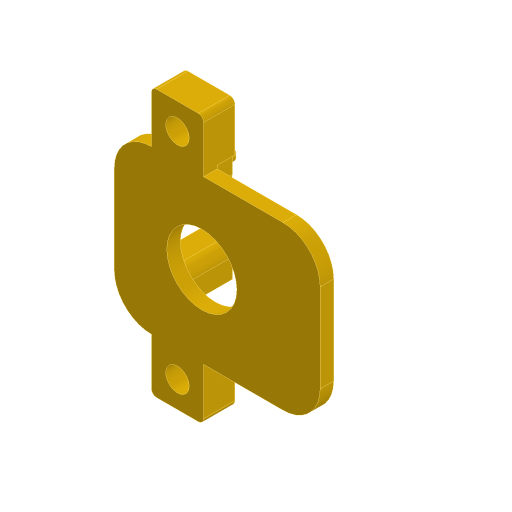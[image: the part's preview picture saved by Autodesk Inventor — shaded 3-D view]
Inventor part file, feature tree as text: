
AUTODESK INVENTOR PART (.ipt)
format: ipt  version: 2024.3 (Build 283343000, 343)  size: 441,344 bytes
history: native  units: mm
features: reference x10, sketch x6, extrude x6, other x4, plane x2, projected_geometry x2, fillet x1, chamfer x1, mirror x1
ambient origin geometry x8: Origin, YZ Plane, XZ Plane, XY Plane, X Axis, Y Axis, Z Axis, Center Point
bodies: Solid1 (feature_tree)
feature tree (33):
  plane  "Work Plane1"
  sketch  "Sketch1"  dims[d0=0.6mm d1=1.0mm d2=1.0mm]
  plane  "Work Plane2"
  extrude  "Extrusion1"  Depth=1.0mm
  fillet  "Fillet1"  Radius=1.0mm
  extrude  "Extrusion2"  Depth=2.0mm
  chamfer  "Chamfer1"  Distance=3.0mm
  extrude  "Extrusion3"  Depth=2.6mm TaperAngle=0.0deg
  extrude  "Extrusion4"  TaperAngle=0.0deg  [1 undecoded]
  extrude  "Extrusion5"  Depth=0.6mm TaperAngle=0.0deg
  extrude  "Extrusion6"  [1 undecoded]
  mirror  "Mirror1"
  reference  "Reference1"
  reference  "Reference2"
  reference  "Reference3"
  sketch  "Sketch2"  dims[d3=10.0mm d4=0.0mm d5=2.0mm d6=3.0mm d7=0.0mm]
  reference  "Reference4"
  reference  "Reference5"
  sketch  "Sketch3"  dims[d8=0.6mm d9=2.0mm d10=45.0deg d11=2.6mm d12=0.0mm]
  reference  "Reference6"
  reference  "Reference7"
  sketch  "Sketch4"  dims[d13=1.0mm d14=0.0mm d15=0.0mm]
  reference  "Reference8"
  sketch  "Sketch5"  dims[d16=6.0mm d17=0.0mm d18=0.6mm d19=0.0mm]
  projected_geometry  "Projected Loop1"
  reference  "Reference9"
  reference  "Reference10"
  sketch  "Sketch6"
  projected_geometry  "Projected Loop2"
  parser-record x1  (decoder bookkeeping rows leaked as tree rows — omitted from the tree; the rows remain in map.json)
  other  "PrzyciskSTOP.iam"
  other  "PrzyciskSTOP_1:1"
  other  "DF Robot DFR0029-R:1"
note: 2 required parameter values undecoded (feature->parameter linkage not recoverable at this tier; creation-order binding heuristic only, values carry confidence <= 0.55)
note: 1 file-system path scrubbed to <path> (originals preserved in map.json)
